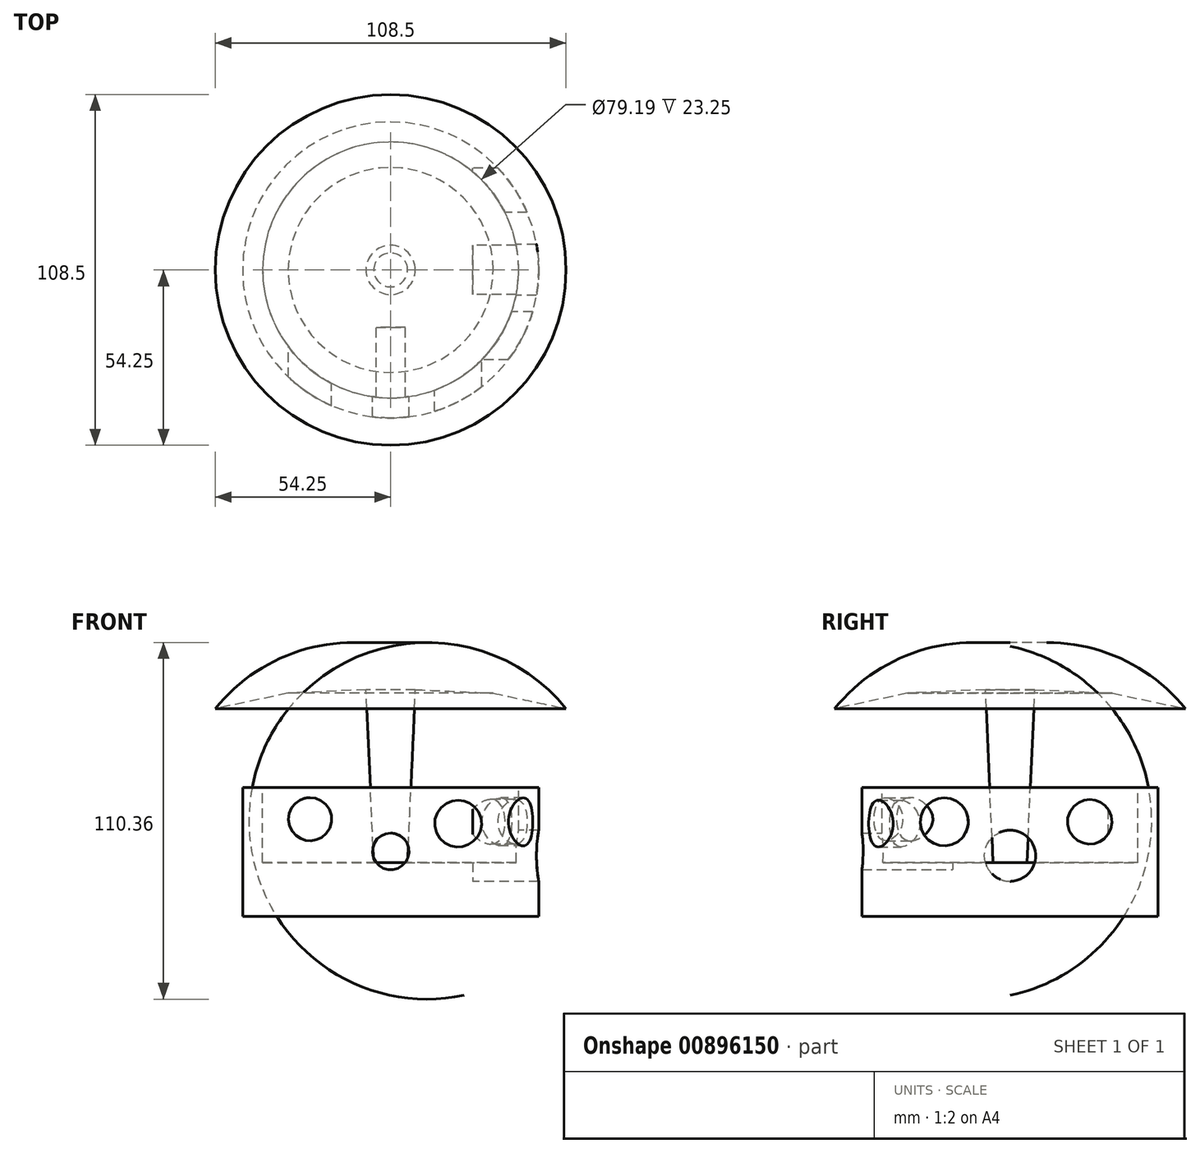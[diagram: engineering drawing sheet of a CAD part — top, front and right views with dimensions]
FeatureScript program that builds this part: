
annotation { "Feature Type Name" : "Feature", "Feature Type Description" : "" }
export const myFeature = defineFeature(function(context is Context, id is Id, definition is map)
    precondition{}
    {
        {
            var Q0;
            Q0=qCreatedBy(makeId("Front.planeOp"),FACE);
            var sketch = newSketch(context, id + "F0", { "sketchPlane" : qUnion([Q0])});
            skLineSegment(sketch, "E0.left", {"start": v(-45.8, -23.25) * mm, "end": v(-45.8, -39.88) * mm});
            skLineSegment(sketch, "E1", {"start": v(-54.25, 24.38) * mm, "end": v(-31.7, 29.17) * mm});
            skLineSegment(sketch, "E2", {"start": v(-31.7, 29.17) * mm, "end": v(-7.62, 30.24) * mm});
            skLineSegment(sketch, "E3", {"start": v(-45.8, -23.25) * mm, "end": v(-45.8, 0) * mm});
            skLineSegment(sketch, "E4", {"start": v(-45.8, 0) * mm, "end": v(-39.6, 0) * mm});
            skLineSegment(sketch, "E5", {"start": v(-39.6, 0) * mm, "end": v(-39.6, -23.25) * mm});
            skLineSegment(sketch, "E6", {"start": v(-45.8, -39.88) * mm, "end": v(0, -39.88) * mm});
            skLineSegment(sketch, "E7", {"start": v(-39.6, -23.25) * mm, "end": v(-5.24, -23.25) * mm});
            skLineSegment(sketch, "E8", {"start": v(0, -23.25) * mm, "end": v(0, -39.88) * mm});
            skArc(sketch, "E9", {"start": v(0, 43.67) * mm, "mid": v(-29.84, 41.66) * mm, "end": v(-54.25, 24.38) * mm});
            skLineSegment(sketch, "E10", {"start": v(-7.62, 30.24) * mm, "end": v(-5.24, -23.25) * mm});
            skPoint(sketch, "E11.start.orphan", {"position": v(0, 30.58) * mm});
            skLineSegment(sketch, "E12", {"start": v(0, 43.67) * mm, "end": v(0, -23.25) * mm});
            skLineSegment(sketch, "E13", {"start": v(0, 60.73) * mm, "end": v(0, -66.09) * mm});
            skSolve(sketch);
        }
        {
            var Q0;
            Q0 = qSketchRegion(id + "F0", true);
            var Q1;
            Q1=sQuery(id+"F0.wireOp",EDGE,"E13");
            revolve(context, id + "F1", {"surfaceOperationType" : NewSurfaceOperationType.NEW, "entities" : qUnion([Q0]), "axis" : qUnion([Q1]), "revolveType" : RevolveType.FULL});
        }
        {
            var Q0;
            Q0=qCreatedBy(makeId("Front.planeOp"),FACE);
            cPlane(context, id + "F2", {"entities" : qUnion([Q0]), "cplaneType" : CPlaneType.OFFSET, "offset" : 17.78 * mm, "width" : 152.4 * mm, "height" : 152.4 * mm});
        }
        {
            var Q0;
            Q0=qCreatedBy(id+"F2.planeOp",FACE);
            var sketch = newSketch(context, id + "F3", { "sketchPlane" : qUnion([Q0])});
            skCircle(sketch, "E14", {"center": v(0, -19.8) * mm, "radius": 5.67 * mm});
            skCircle(sketch, "E15", {"center": v(20.88, -11.18) * mm, "radius": 7.25 * mm});
            skCircle(sketch, "E16", {"center": v(-24.92, -9.83) * mm, "radius": 6.67 * mm});
            skSolve(sketch);
        }
        {
            var Q0;
            Q0 = qSketchRegion(id + "F3", true);
            extrude(context, id + "F4", {"entities" : qUnion([Q0]), "operationType" : NewBodyOperationType.REMOVE, "depth" : 127 * mm, "offsetDistance" : 25.4 * mm});
        }
        {
            var Q0;
            Q0=qCreatedBy(makeId("Right.planeOp"),FACE);
            cPlane(context, id + "F5", {"entities" : qUnion([Q0]), "cplaneType" : CPlaneType.OFFSET, "offset" : 25.4 * mm, "width" : 152.4 * mm, "height" : 152.4 * mm});
        }
        {
            var Q0;
            Q0=qCreatedBy(id+"F5.planeOp",FACE);
            var sketch = newSketch(context, id + "F6", { "sketchPlane" : qUnion([Q0])});
            skCircle(sketch, "E17", {"center": v(0, -21.15) * mm, "radius": 7.91 * mm});
            skCircle(sketch, "E18", {"center": v(-20.34, -10.64) * mm, "radius": 7.43 * mm});
            skCircle(sketch, "E19", {"center": v(24.65, -10.64) * mm, "radius": 6.88 * mm});
            skSolve(sketch);
        }
        {
            var Q0;
            Q0 = qSketchRegion(id + "F6", true);
            extrude(context, id + "F7", {"entities" : qUnion([Q0]), "operationType" : NewBodyOperationType.REMOVE, "depth" : 25.4 * mm, "offsetDistance" : 25.4 * mm});
        }
    });
